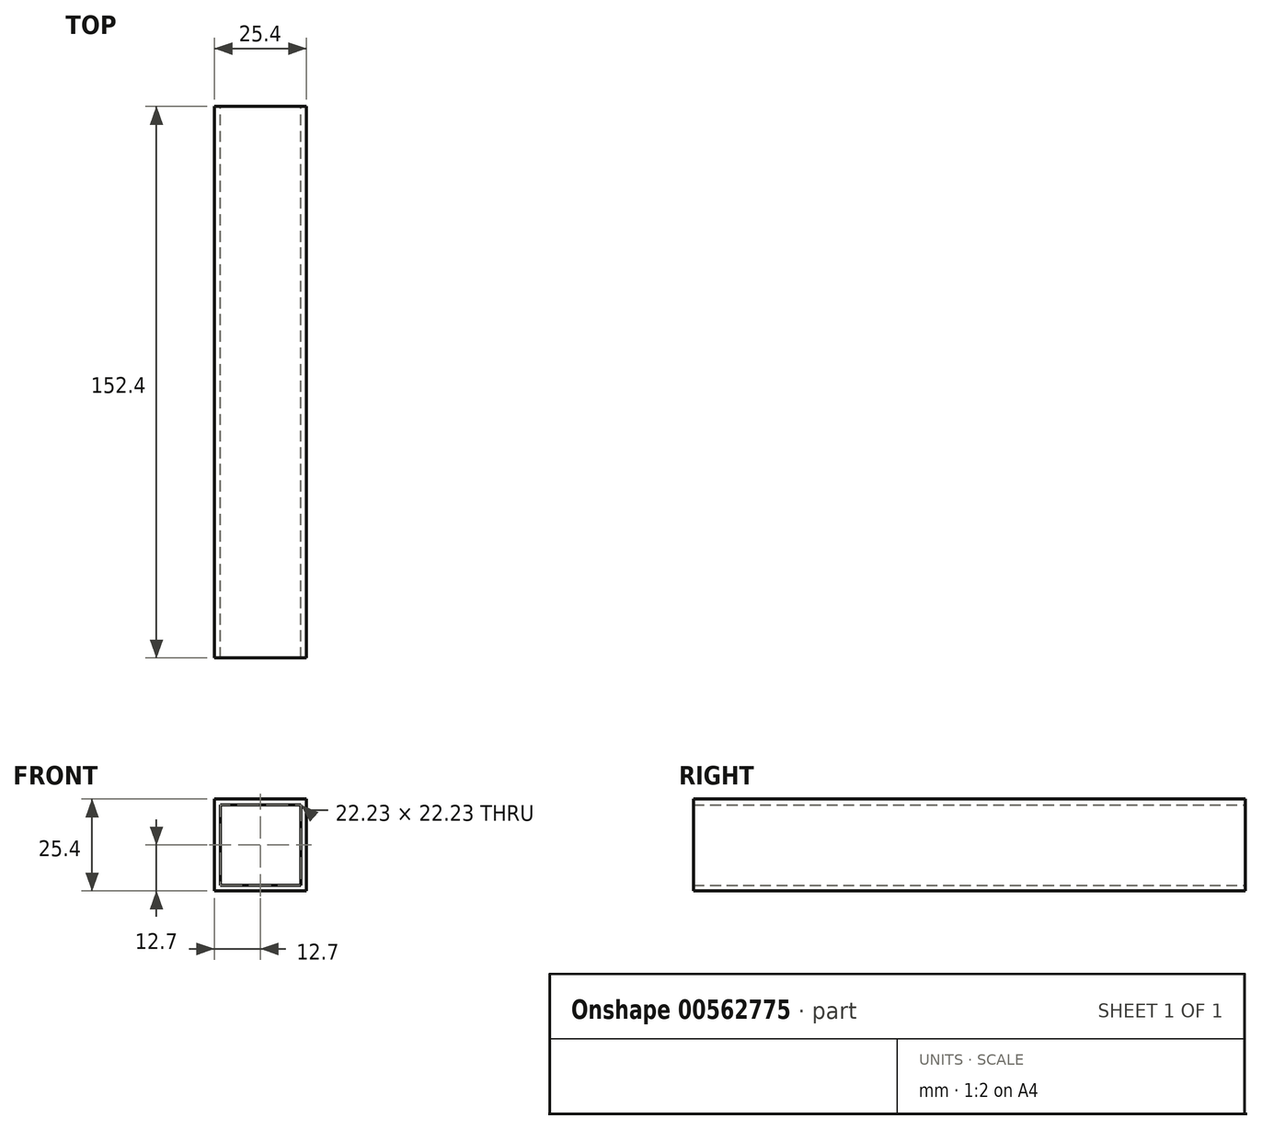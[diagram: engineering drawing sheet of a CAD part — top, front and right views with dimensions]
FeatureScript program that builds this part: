
annotation { "Feature Type Name" : "Feature", "Feature Type Description" : "" }
export const myFeature = defineFeature(function(context is Context, id is Id, definition is map)
    precondition{}
    {
        {
            var Q0;
            Q0=qCreatedBy(makeId("Front.planeOp"),FACE);
            var sketch = newSketch(context, id + "F0", { "sketchPlane" : qUnion([Q0])});
            skLineSegment(sketch, "E0.bottom", {"start": v(-12.7, 12.7) * mm, "end": v(12.7, 12.7) * mm});
            skLineSegment(sketch, "E0.top", {"start": v(-12.7, -12.7) * mm, "end": v(12.7, -12.7) * mm});
            skLineSegment(sketch, "E0.left", {"start": v(-12.7, 12.7) * mm, "end": v(-12.7, -12.7) * mm});
            skLineSegment(sketch, "E0.right", {"start": v(12.7, 12.7) * mm, "end": v(12.7, -12.7) * mm});
            skPoint(sketch, "E0.middle", {"position": v(0, 0) * mm});
            skLineSegment(sketch, "E1.0", {"start": v(-11.11, 11.11) * mm, "end": v(11.11, 11.11) * mm});
            skLineSegment(sketch, "E1.1", {"start": v(-11.11, 11.11) * mm, "end": v(-11.11, -11.11) * mm});
            skLineSegment(sketch, "E1.2", {"start": v(-11.11, -11.11) * mm, "end": v(11.11, -11.11) * mm});
            skLineSegment(sketch, "E1.3", {"start": v(11.11, 11.11) * mm, "end": v(11.11, -11.11) * mm});
            skSolve(sketch);
        }
        {
            var Q0;
            Q0 = qSketchRegion(id + "F0", true);
            extrude(context, id + "F1", {"entities" : qUnion([Q0]), "depth" : 152.4 * mm, "offsetDistance" : 25.4 * mm});
        }
    });
